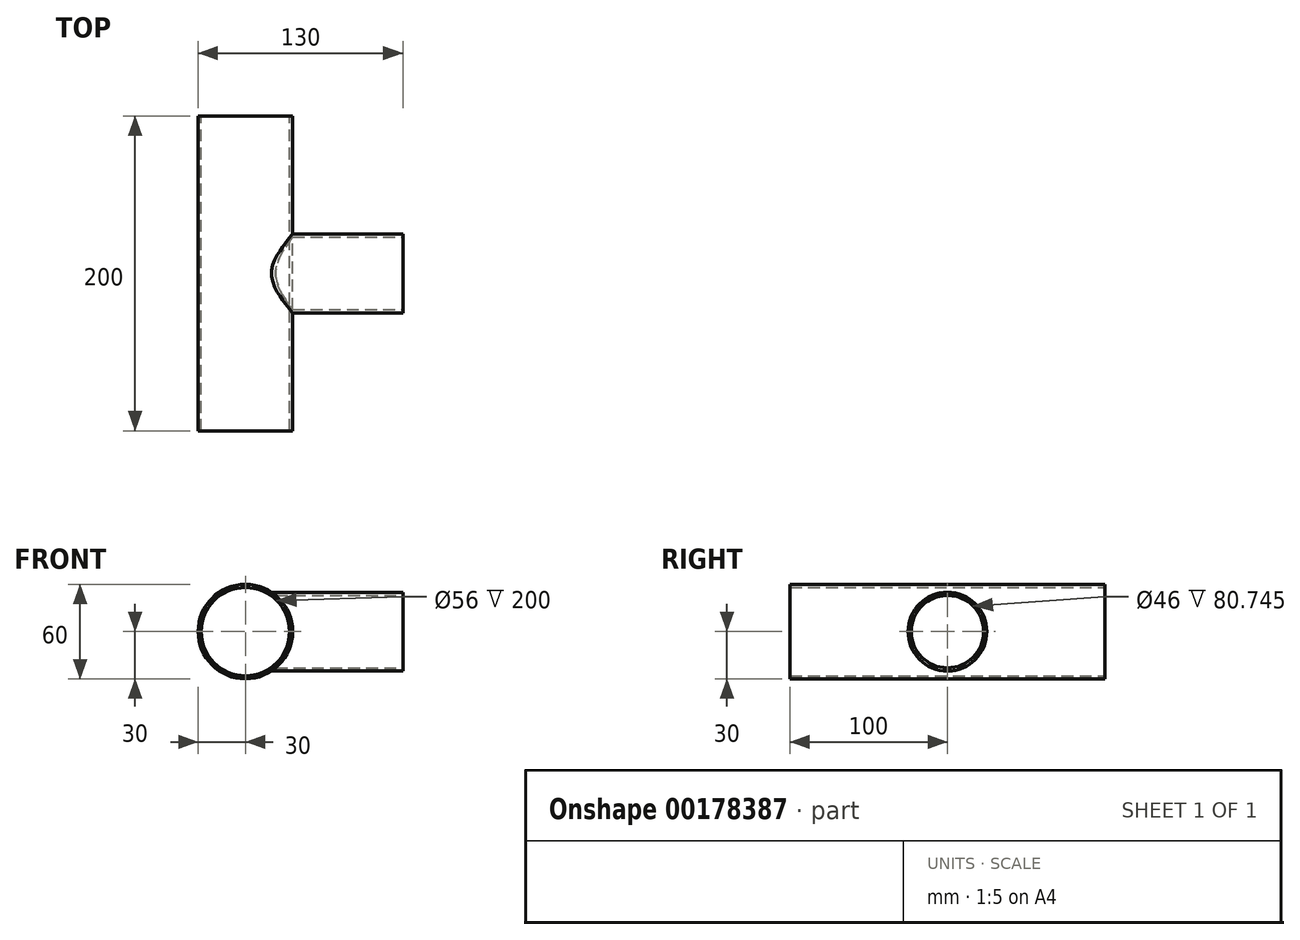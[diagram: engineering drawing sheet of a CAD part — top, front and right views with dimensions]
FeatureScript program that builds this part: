
annotation { "Feature Type Name" : "Feature", "Feature Type Description" : "" }
export const myFeature = defineFeature(function(context is Context, id is Id, definition is map)
    precondition{}
    {
        {
            var Q0;
            Q0=qCreatedBy(makeId("Front.planeOp"),FACE);
            var sketch = newSketch(context, id + "F0", { "sketchPlane" : qUnion([Q0])});
            skCircle(sketch, "E0", {"center": v(0, 0) * mm, "radius": 30 * mm});
            skCircle(sketch, "E1.0", {"center": v(0, 0) * mm, "radius": 28 * mm});
            skSolve(sketch);
        }
        {
            var Q0;
            Q0=makeQuery(id+"F0.imprint","IMPRINT",FACE,{"disambiguationData":[TD([[makeQuery(id+"F0.imprint","IMPRINT",EDGE,{"derivedFrom":sQuery(id+"F0.wireOp",EDGE,"E0")}),1.0]])]});
            extrude(context, id + "F1", {"entities" : qUnion([Q0]), "depth" : 200 * mm});
        }
        {
            var Q0;
            Q0=qCreatedBy(makeId("Right.planeOp"),FACE);
            cPlane(context, id + "F2", {"entities" : qUnion([Q0]), "cplaneType" : CPlaneType.OFFSET, "offset" : 100 * mm, "width" : 150 * mm, "height" : 150 * mm});
        }
        {
            var Q0;
            Q0=qCreatedBy(id+"F2.planeOp",FACE);
            var sketch = newSketch(context, id + "F3", { "sketchPlane" : qUnion([Q0])});
            skLineSegment(sketch, "E2.0", {"start": v(-200, -30) * mm, "end": v(-200, 30) * mm});
            skLineSegment(sketch, "E3.0", {"start": v(0, -30) * mm, "end": v(0, 30) * mm});
            skLineSegment(sketch, "E4", {"start": v(-200, 30) * mm, "end": v(0, 30) * mm});
            skLineSegment(sketch, "E5", {"start": v(0, -30) * mm, "end": v(-200, -30) * mm});
            skPoint(sketch, "E6", {"position": v(-100, 0) * mm});
            skPoint(sketch, "E6.positionSnap0", {"position": v(-200, 0) * mm});
            skPoint(sketch, "E7", {"position": v(-100, 30) * mm});
            skCircle(sketch, "E8", {"center": v(-100, 0) * mm, "radius": 25 * mm});
            skCircle(sketch, "E9.0", {"center": v(-100, 0) * mm, "radius": 23 * mm});
            skSolve(sketch);
        }
        {
            var Q0;
            Q0=makeQuery(id+"F3.imprint","IMPRINT",FACE,{"disambiguationData":[TD([[makeQuery(id+"F3.imprint","IMPRINT",EDGE,{"derivedFrom":sQuery(id+"F3.wireOp",EDGE,"E8")}),1.0]])]});
            extrude(context, id + "F4", {"entities" : qUnion([Q0]), "operationType" : NewBodyOperationType.ADD, "endBound" : BoundingType.UP_TO_NEXT, "oppositeDirection" : true, "depth" : 25 * mm});
        }
    });
